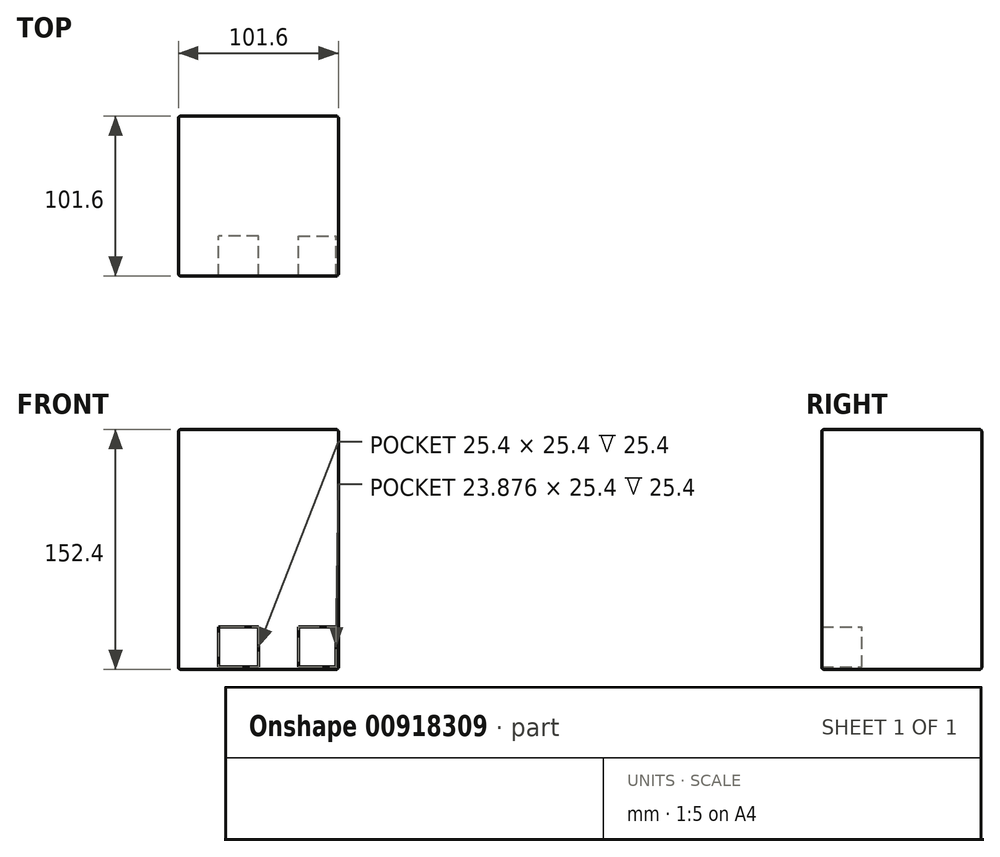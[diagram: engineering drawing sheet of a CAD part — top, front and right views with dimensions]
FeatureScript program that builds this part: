
annotation { "Feature Type Name" : "Feature", "Feature Type Description" : "" }
export const myFeature = defineFeature(function(context is Context, id is Id, definition is map)
    precondition{}
    {
        {
            var Q0;
            Q0=qCreatedBy(makeId("Top.planeOp"),FACE);
            var sketch = newSketch(context, id + "F0", { "sketchPlane" : qUnion([Q0])});
            skLineSegment(sketch, "E0.bottom", {"start": v(50.8, 50.8) * mm, "end": v(-50.8, 50.8) * mm});
            skLineSegment(sketch, "E0.top", {"start": v(50.8, -50.8) * mm, "end": v(-50.8, -50.8) * mm});
            skLineSegment(sketch, "E0.left", {"start": v(50.8, 50.8) * mm, "end": v(50.8, -50.8) * mm});
            skLineSegment(sketch, "E0.right", {"start": v(-50.8, 50.8) * mm, "end": v(-50.8, -50.8) * mm});
            skPoint(sketch, "E0.middle", {"position": v(0, 0) * mm});
            skSolve(sketch);
        }
        {
            var Q0;
            Q0=makeQuery(id+"F0.imprint","IMPRINT",FACE,{"disambiguationData":[TD([[makeQuery(id+"F0.imprint","IMPRINT",EDGE,{"derivedFrom":sQuery(id+"F0.wireOp",EDGE,"E0.bottom")}),1.0]])]});
            extrude(context, id + "F1", {"entities" : qUnion([Q0]), "depth" : 152.4 * mm, "offsetDistance" : 25.4 * mm});
        }
        {
            var Q0;
            Q0=makeQuery(id+"F1.opExtrude","SWEPT_FACE",FACE,{"disambiguationData":[OSD([sQuery(id+"F0.wireOp",EDGE,"E0.top")])]});
            var Q1;
            Q1=makeQuery(id+"F1.opExtrude","SWEPT_FACE",FACE,{"disambiguationData":[OSD([sQuery(id+"F0.wireOp",EDGE,"E0.bottom")])]});
            var Q2;
            Q2=makeQuery(id+"F1.opExtrude","CAP_FACE",FACE,{"disambiguationData":[OSD([sQuery(id+"F0.wireOp",EDGE,"E0.bottom"),sQuery(id+"F0.wireOp",EDGE,"E0.top"),sQuery(id+"F0.wireOp",EDGE,"E0.left"),sQuery(id+"F0.wireOp",EDGE,"E0.right")])],"isStart":false});
            var Q3;
            Q3=makeQuery(id+"F1.opExtrude","CAP_FACE",FACE,{"disambiguationData":[OSD([sQuery(id+"F0.wireOp",EDGE,"E0.bottom"),sQuery(id+"F0.wireOp",EDGE,"E0.top"),sQuery(id+"F0.wireOp",EDGE,"E0.left"),sQuery(id+"F0.wireOp",EDGE,"E0.right")])],"isStart":true});
            fillet(context, id + "F2", {"entities" : qUnion([Q0, Q1, Q2, Q3]), "radius" : 1.52 * mm, "tangentPropagation" : true, "allowEdgeOverflow" : false});
        }
        {
            var Q0;
            Q0=makeQuery(id+"F1.opExtrude","SWEPT_FACE",FACE,{"disambiguationData":[OSD([sQuery(id+"F0.wireOp",EDGE,"E0.top")])]});
            var sketch = newSketch(context, id + "F3", { "sketchPlane" : qUnion([Q0])});
            skLineSegment(sketch, "E1.bottom", {"start": v(-49.28, 1.52) * mm, "end": v(-25.4, 1.52) * mm});
            skLineSegment(sketch, "E1.top", {"start": v(-49.28, 26.92) * mm, "end": v(-25.4, 26.92) * mm});
            skLineSegment(sketch, "E1.left", {"start": v(-49.28, 1.52) * mm, "end": v(-49.28, 26.92) * mm});
            skLineSegment(sketch, "E1.right", {"start": v(-25.4, 1.52) * mm, "end": v(-25.4, 26.92) * mm});
            skLineSegment(sketch, "E2.bottom", {"start": v(-25.4, 26.92) * mm, "end": v(0, 26.92) * mm});
            skLineSegment(sketch, "E2.top", {"start": v(-25.4, 1.52) * mm, "end": v(0, 1.52) * mm});
            skLineSegment(sketch, "E2.left", {"start": v(-25.4, 26.92) * mm, "end": v(-25.4, 1.52) * mm});
            skLineSegment(sketch, "E2.right", {"start": v(0, 26.92) * mm, "end": v(0, 1.52) * mm});
            skLineSegment(sketch, "E3.bottom", {"start": v(0, 26.92) * mm, "end": v(25.4, 26.92) * mm});
            skLineSegment(sketch, "E3.top", {"start": v(0, 1.52) * mm, "end": v(25.4, 1.52) * mm});
            skLineSegment(sketch, "E3.right", {"start": v(25.4, 26.92) * mm, "end": v(25.4, 1.52) * mm});
            skLineSegment(sketch, "E4.bottom", {"start": v(25.4, 26.92) * mm, "end": v(49.28, 26.92) * mm});
            skLineSegment(sketch, "E4.top", {"start": v(25.4, 1.52) * mm, "end": v(49.28, 1.52) * mm});
            skLineSegment(sketch, "E4.right", {"start": v(49.28, 26.92) * mm, "end": v(49.28, 1.52) * mm});
            skSolve(sketch);
        }
        {
            var Q0;
            Q0=makeQuery(id+"F3.imprint","IMPRINT",FACE,{"disambiguationData":[TD([[makeQuery(id+"F3.imprint","IMPRINT",EDGE,{"derivedFrom":sQuery(id+"F3.wireOp",EDGE,"E2.bottom")}),-1.0]])]});
            var Q1;
            Q1=makeQuery(id+"F3.imprint","IMPRINT",FACE,{"disambiguationData":[TD([[makeQuery(id+"F3.imprint","IMPRINT",EDGE,{"derivedFrom":sQuery(id+"F3.wireOp",EDGE,"E4.bottom")}),-1.0]])]});
            extrude(context, id + "F4", {"entities" : qUnion([Q0, Q1]), "operationType" : NewBodyOperationType.REMOVE, "oppositeDirection" : true, "depth" : 25.4 * mm, "offsetDistance" : 25.4 * mm});
        }
        {
            var Q0;
            Q0=makeQuery(id+"F4.boolean.opBoolean","COPY",FACE,{"derivedFrom":makeQuery(id+"F4.opExtrude","CAP_FACE",FACE,{"disambiguationData":[OSD([sQuery(id+"F3.wireOp",EDGE,"E4.bottom"),sQuery(id+"F3.wireOp",EDGE,"E4.top"),sQuery(id+"F3.wireOp",EDGE,"E3.right"),sQuery(id+"F3.wireOp",EDGE,"E4.right")])],"isStart":false})});
            var Q1;
            Q1=makeQuery(id+"F4.boolean.opBoolean","COPY",FACE,{"derivedFrom":makeQuery(id+"F4.opExtrude","CAP_FACE",FACE,{"disambiguationData":[OSD([sQuery(id+"F3.wireOp",EDGE,"E2.bottom"),sQuery(id+"F3.wireOp",EDGE,"E2.top"),sQuery(id+"F3.wireOp",EDGE,"E2.left"),sQuery(id+"F3.wireOp",EDGE,"E2.right")])],"isStart":false})});
            extrude(context, id + "F5", {"entities" : qUnion([Q0, Q1]), "depth" : 25.4 * mm, "offsetDistance" : 25.4 * mm});
        }
    });
